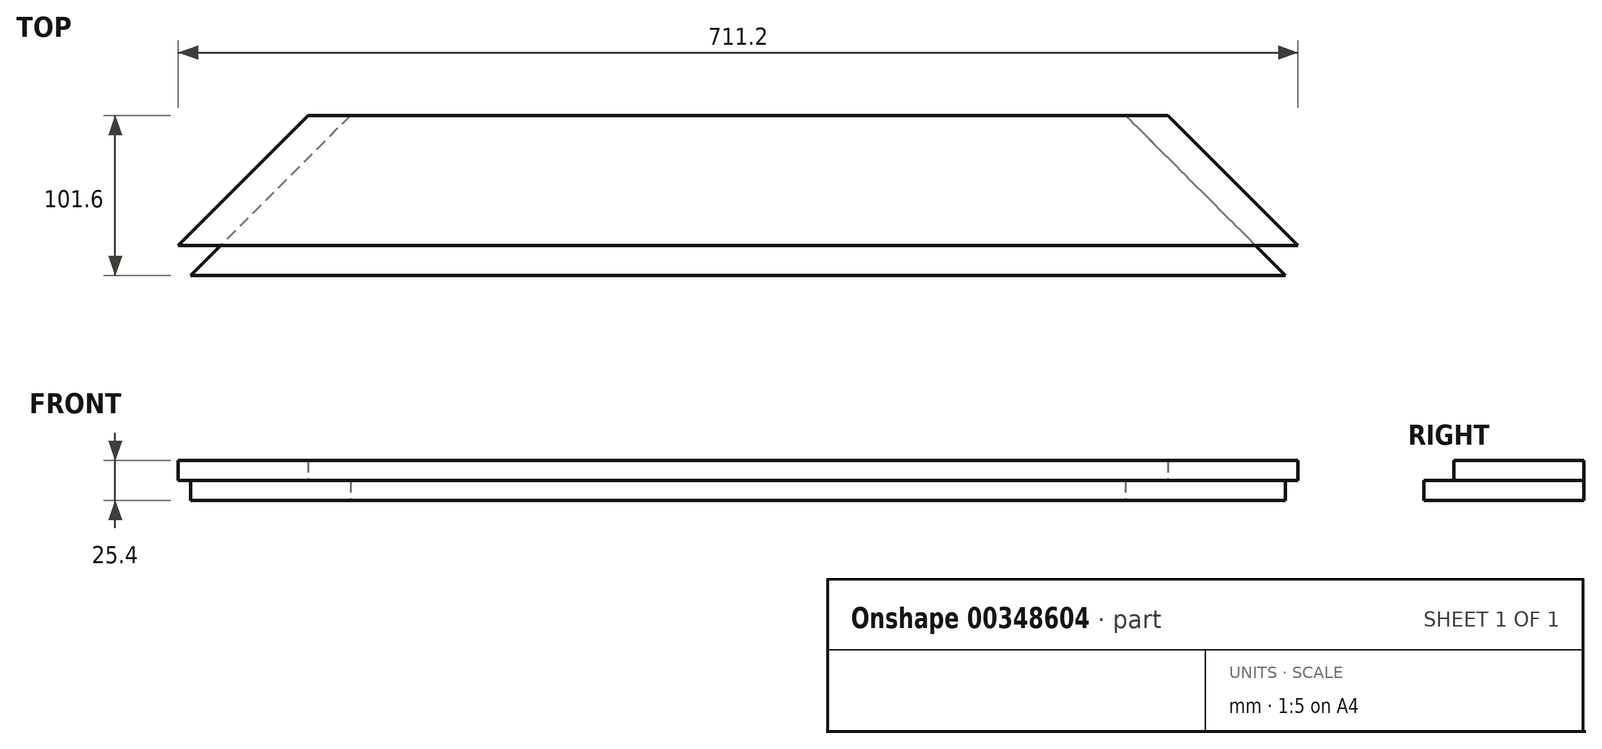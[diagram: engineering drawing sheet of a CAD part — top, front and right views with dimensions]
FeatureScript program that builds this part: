
annotation { "Feature Type Name" : "Feature", "Feature Type Description" : "" }
export const myFeature = defineFeature(function(context is Context, id is Id, definition is map)
    precondition{}
    {
        {
            var Q0;
            Q0=qCreatedBy(makeId("Top.planeOp"),FACE);
            var sketch = newSketch(context, id + "F0", { "sketchPlane" : qUnion([Q0])});
            skLineSegment(sketch, "E0", {"start": v(-457.77, 87.9) * mm, "end": v(88.33, 87.9) * mm});
            skLineSegment(sketch, "E1", {"start": v(88.33, 87.9) * mm, "end": v(189.93, -13.7) * mm});
            skLineSegment(sketch, "E2", {"start": v(189.93, -13.7) * mm, "end": v(-559.37, -13.7) * mm});
            skLineSegment(sketch, "E3", {"start": v(-559.37, -13.7) * mm, "end": v(-457.77, 87.9) * mm});
            skLineSegment(sketch, "E4", {"start": v(-540.32, 5.35) * mm, "end": v(170.88, 5.35) * mm});
            skLineSegment(sketch, "E5", {"start": v(-430.83, 87.9) * mm, "end": v(-532.43, -13.7) * mm});
            skLineSegment(sketch, "E6", {"start": v(163, -13.7) * mm, "end": v(61.4, 87.9) * mm});
            skSolve(sketch);
        }
        {
            var Q0;
            {var subQ0=sQuery(id+"F0.wireOp",EDGE,"E5");var subQ1=sQuery(id+"F0.wireOp",EDGE,"E0");var subQ2=makeQuery(id+"F0.imprint","INTERSECT",VERTEX,{"derivedFrom":[subQ1,subQ0]});Q0=makeQuery(id+"F0.imprint","IMPRINT",FACE,{"disambiguationData":[TD([[makeQuery(id+"F0.imprint","IMPRINT",EDGE,{"disambiguationData":[TD([[subQ2,-1.0]])],"derivedFrom":subQ1}),-1.0]])]});}
            var Q1;
            {var subQ0=sQuery(id+"F0.wireOp",EDGE,"E3");var subQ1=sQuery(id+"F0.wireOp",EDGE,"E0");var subQ2=makeQuery(id+"F0.imprint","INTERSECT",VERTEX,{"derivedFrom":[subQ1,subQ0]});Q1=makeQuery(id+"F0.imprint","IMPRINT",FACE,{"disambiguationData":[TD([[makeQuery(id+"F0.imprint","IMPRINT",EDGE,{"disambiguationData":[TD([[subQ2,-1.0]])],"derivedFrom":subQ1}),-1.0]])]});}
            var Q2;
            {var subQ0=sQuery(id+"F0.wireOp",EDGE,"E5");var subQ1=sQuery(id+"F0.wireOp",EDGE,"E2");var subQ2=makeQuery(id+"F0.imprint","INTERSECT",VERTEX,{"derivedFrom":[subQ1,subQ0]});Q2=makeQuery(id+"F0.imprint","IMPRINT",FACE,{"disambiguationData":[TD([[makeQuery(id+"F0.imprint","IMPRINT",EDGE,{"disambiguationData":[TD([[subQ2,1.0]])],"derivedFrom":subQ1}),-1.0]])]});}
            var Q3;
            {var subQ0=sQuery(id+"F0.wireOp",EDGE,"E1");var subQ1=sQuery(id+"F0.wireOp",EDGE,"E0");var subQ2=makeQuery(id+"F0.imprint","INTERSECT",VERTEX,{"derivedFrom":[subQ1,subQ0]});Q3=makeQuery(id+"F0.imprint","IMPRINT",FACE,{"disambiguationData":[TD([[makeQuery(id+"F0.imprint","IMPRINT",EDGE,{"disambiguationData":[TD([[subQ2,1.0]])],"derivedFrom":subQ1}),-1.0]])]});}
            extrude(context, id + "F1", {"entities" : qUnion([Q0, Q1, Q2, Q3]), "depth" : 12.7 * mm});
        }
        {
            var Q0;
            {var subQ0=sQuery(id+"F0.wireOp",EDGE,"E5");var subQ1=sQuery(id+"F0.wireOp",EDGE,"E0");var subQ2=makeQuery(id+"F0.imprint","INTERSECT",VERTEX,{"derivedFrom":[subQ1,subQ0]});Q0=makeQuery(id+"F0.imprint","IMPRINT",FACE,{"disambiguationData":[TD([[makeQuery(id+"F0.imprint","IMPRINT",EDGE,{"disambiguationData":[TD([[subQ2,-1.0]])],"derivedFrom":subQ1}),-1.0]])]});}
            var Q1;
            {var subQ0=sQuery(id+"F0.wireOp",EDGE,"E3");var subQ1=sQuery(id+"F0.wireOp",EDGE,"E0");var subQ2=makeQuery(id+"F0.imprint","INTERSECT",VERTEX,{"derivedFrom":[subQ1,subQ0]});Q1=makeQuery(id+"F0.imprint","IMPRINT",FACE,{"disambiguationData":[TD([[makeQuery(id+"F0.imprint","IMPRINT",EDGE,{"disambiguationData":[TD([[subQ2,-1.0]])],"derivedFrom":subQ1}),-1.0]])]});}
            var Q2;
            {var subQ0=sQuery(id+"F0.wireOp",EDGE,"E1");var subQ1=sQuery(id+"F0.wireOp",EDGE,"E0");var subQ2=makeQuery(id+"F0.imprint","INTERSECT",VERTEX,{"derivedFrom":[subQ1,subQ0]});Q2=makeQuery(id+"F0.imprint","IMPRINT",FACE,{"disambiguationData":[TD([[makeQuery(id+"F0.imprint","IMPRINT",EDGE,{"disambiguationData":[TD([[subQ2,1.0]])],"derivedFrom":subQ1}),-1.0]])]});}
            extrude(context, id + "F2", {"entities" : qUnion([Q0, Q1, Q2]), "operationType" : NewBodyOperationType.ADD, "depth" : 25.4 * mm});
        }
        {
            var Q0;
            {var subQ0=sQuery(id+"F0.wireOp",EDGE,"E1");var subQ1=sQuery(id+"F0.wireOp",EDGE,"E0");var subQ2=makeQuery(id+"F0.imprint","INTERSECT",VERTEX,{"derivedFrom":[subQ1,subQ0]});Q0=makeQuery(id+"F0.imprint","IMPRINT",FACE,{"disambiguationData":[TD([[makeQuery(id+"F0.imprint","IMPRINT",EDGE,{"disambiguationData":[TD([[subQ2,1.0]])],"derivedFrom":subQ1}),-1.0]])]});}
            var Q1;
            {var subQ0=sQuery(id+"F0.wireOp",EDGE,"E3");var subQ1=sQuery(id+"F0.wireOp",EDGE,"E0");var subQ2=makeQuery(id+"F0.imprint","INTERSECT",VERTEX,{"derivedFrom":[subQ1,subQ0]});Q1=makeQuery(id+"F0.imprint","IMPRINT",FACE,{"disambiguationData":[TD([[makeQuery(id+"F0.imprint","IMPRINT",EDGE,{"disambiguationData":[TD([[subQ2,-1.0]])],"derivedFrom":subQ1}),-1.0]])]});}
            extrude(context, id + "F3", {"entities" : qUnion([Q0, Q1]), "operationType" : NewBodyOperationType.REMOVE, "oppositeDirection" : true, "depth" : -12.7 * mm});
        }
    });
